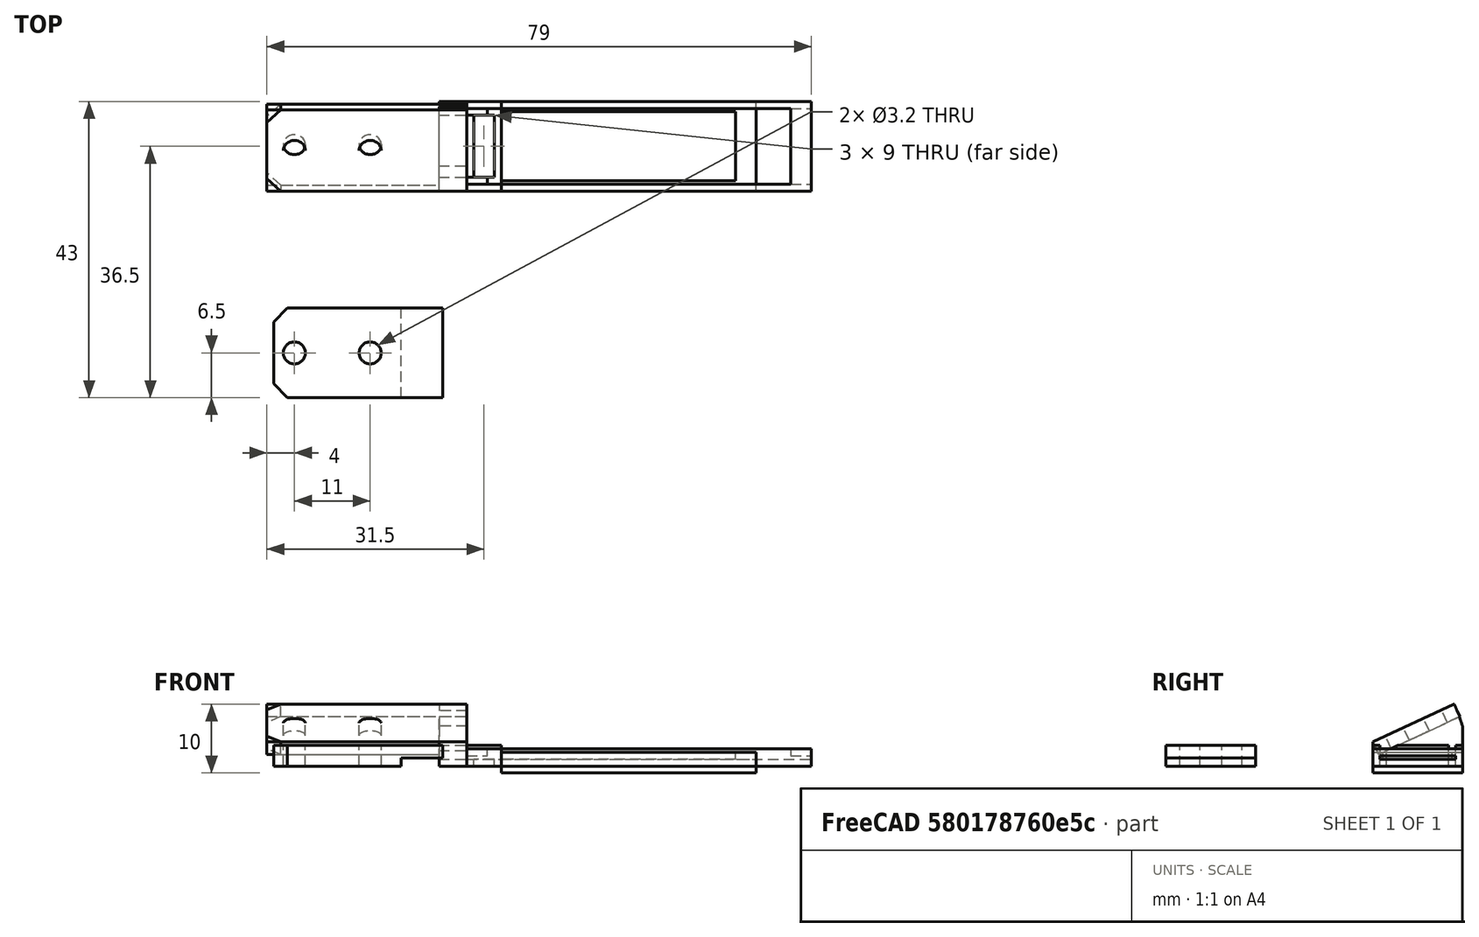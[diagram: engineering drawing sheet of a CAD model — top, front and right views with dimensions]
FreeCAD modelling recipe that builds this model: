
FCSTD DOCUMENT  (FreeCAD 0.18R14555 (Git shallow))
Label: neopixel-mount-bottom
License: All rights reserved
LicenseURL: http://en.wikipedia.org/wiki/All_rights_reserved
objects: Part::Box×18, Part::Cut×9, Part::Cylinder×5, Part::MultiFuse×3, Part::Chamfer×2, Part::Feature×1
note: 38 computed .brp shape members not serialized (recipe doc carries the construction recipe); baked Part::Feature solids carry a one-line shape summary decoded from their .brp

FEATURE [Part::Box] Box  label="Cube"
  AttacherType = Attacher::AttachEngine3D
  Height = 1
  Length = 37
  Width = 11
FEATURE [Part::Box] Box001  label="Cube001"
  AttacherType = Attacher::AttachEngine3D
  Height = 3
  Length = 37
  Placement = pos=(0,-1,-1) rot=(0,0,1;0rad)
  Width = 13
FEATURE [Part::Box] Box002  label="Cube002"
  AttacherType = Attacher::AttachEngine3D
  Height = 3
  Length = 34
  Placement = pos=(0,0.5,0) rot=(0,0,1;0rad)
  Width = 10
FEATURE [Part::Cut] Cut
  Base = -> Box001
  Tool = -> Box
FEATURE [Part::Cut] Cut001
  Base = -> Cut
  Tool = -> Box002
FEATURE [Part::Box] Box003  label="Cube003"
  AttacherType = Attacher::AttachEngine3D
  Height = 3
  Length = 5
  Placement = pos=(-5,-1,-1) rot=(0,0,1;0rad)
  Width = 13
FEATURE [Part::Box] Box004  label="Cube004"
  AttacherType = Attacher::AttachEngine3D
  Height = 2
  Length = 5
  Placement = pos=(-5,0,0) rot=(0,0,1;0rad)
  Width = 11
FEATURE [Part::Cut] Cut002
  Base = -> Box003
  Tool = -> Box004
FEATURE [Part::Box] Box005  label="Cube005"
  AttacherType = Attacher::AttachEngine3D
  Height = 10
  Length = 3
  Placement = pos=(-4,1,-1) rot=(0,0,1;0rad)
  Width = 9
FEATURE [Part::Cut] Cut003
  Base = -> Cut002
  Placement = pos=(0,0,1) rot=(0,0,1;0rad)
  Tool = -> Box005
FEATURE [Part::Cylinder] Cylinder
  Angle = 25
  AttacherType = Attacher::AttachEngine3D
  Height = 4
  Placement = pos=(-5,-8.5,-1) rot=(-0.473306,-0.742942,0.473306;1.86366rad)
  Radius = 21.3
FEATURE [Part::Box] Box006  label="Cube006"
  AttacherType = Attacher::AttachEngine3D
  Height = 2
  Length = 29
  Placement = pos=(-38,-1,0) rot=(0,0,1;0rad)
  Width = 13
FEATURE [Part::Cylinder] Cylinder001
  Angle = 360
  AttacherType = Attacher::AttachEngine3D
  Height = 10
  Placement = pos=(-23,5.5,0) rot=(0,0,1;0rad)
  Radius = 1.6
FEATURE [Part::Cylinder] Cylinder002
  Angle = 360
  AttacherType = Attacher::AttachEngine3D
  Height = 10
  Placement = pos=(-34,5.5,0) rot=(0,0,1;0rad)
  Radius = 1.6
FEATURE [Part::MultiFuse] Fusion
  Shapes = -> [Cylinder002,Cylinder001]
FEATURE [Part::Cut] Cut004
  Base = -> Box006
  Placement = pos=(4,0.75,2.11) rot=(1,0,0;0.436332rad)
  Tool = -> Fusion
FEATURE [Part::Box] Box007  label="Cube007"
  AttacherType = Attacher::AttachEngine3D
  Height = 10
  Length = 10
  Placement = pos=(-10.5,-11,-2) rot=(0,0,1;0rad)
  Width = 10
FEATURE [Part::Cut] Cut005
  Base = -> Cylinder
  Tool = -> Box007
FEATURE [Part::Box] Box008  label="Cube008"
  AttacherType = Attacher::AttachEngine3D
  Height = 10
  Length = 10
  Placement = pos=(-10.5,12,-5) rot=(0,0,1;0rad)
  Width = 10
FEATURE [Part::Cut] Cut006
  Base = -> Cut005
  Placement = pos=(0,0,1) rot=(0,0,1;0rad)
  Tool = -> Box008
FEATURE [Part::Box] Box009  label="Cube009"
  AttacherType = Attacher::AttachEngine3D
  Height = 2
  Length = 4
  Placement = pos=(-9,1,1) rot=(0,0,1;0rad)
  Width = 9
FEATURE [Part::Box] Box010  label="Cube010"
  AttacherType = Attacher::AttachEngine3D
  Height = 1
  Length = 50
  Placement = pos=(-5,-1,0) rot=(0,0,1;0rad)
  Width = 13
FEATURE [Part::Cut] Cut007
  Base = -> Cut006
  Tool = -> Box009
FEATURE [Part::Box] Box011  label="Cube011"
  AttacherType = Attacher::AttachEngine3D
  Height = 1
  Length = 3
  Placement = pos=(42,-1,1.5) rot=(0,0,1;0rad)
  Width = 13
FEATURE [Part::Box] Box012  label="Cube012"
  AttacherType = Attacher::AttachEngine3D
  Height = 2.5
  Length = 50
  Placement = pos=(-5,-1,0) rot=(0,0,1;0rad)
  Width = 1
FEATURE [Part::Box] Box013  label="Cube013"
  AttacherType = Attacher::AttachEngine3D
  Height = 2.5
  Length = 50
  Placement = pos=(-5,11,0) rot=(0,0,1;0rad)
  Width = 1
FEATURE [Part::Box] Box014  label="Cube014"
  AttacherType = Attacher::AttachEngine3D
  Height = 1
  Length = 3
  Placement = pos=(-5,-1,1.5) rot=(0,0,1;0rad)
  Width = 2
FEATURE [Part::Box] Box015  label="Cube015"
  AttacherType = Attacher::AttachEngine3D
  Height = 1
  Length = 3
  Placement = pos=(-5,10,1.5) rot=(0,0,1;0rad)
  Width = 2
FEATURE [Part::MultiFuse] Fusion001
  Shapes = -> [Box015,Box014,Box013,Box012,Box011,Cut007,Box010,Cut004]
FEATURE [Part::Feature] Fusion001001  label="Fusion002"
  shape: bbox 79 x 13 x 9.002 mm, 32 faces (baked)
FEATURE [Part::Box] Box016  label="Cube016"
  AttacherType = Attacher::AttachEngine3D
  Height = 3
  Length = 24.5
  Placement = pos=(-33,-31,0) rot=(0,0,1;0rad)
  Width = 13
FEATURE [Part::Box] Box017  label="Cube017"
  AttacherType = Attacher::AttachEngine3D
  Height = 1.2
  Length = 6
  Placement = pos=(-14.5,-31,0) rot=(0,0,1;0rad)
  Width = 13
FEATURE [Part::Cylinder] Cylinder003
  Angle = 360
  AttacherType = Attacher::AttachEngine3D
  Height = 10
  Placement = pos=(-30,-24.5,0) rot=(0,0,1;0rad)
  Radius = 1.6
FEATURE [Part::Cylinder] Cylinder004
  Angle = 360
  AttacherType = Attacher::AttachEngine3D
  Height = 10
  Placement = pos=(-19,-24.5,0) rot=(0,0,1;0rad)
  Radius = 1.6
FEATURE [Part::MultiFuse] Fusion001002
  Shapes = -> [Cylinder003,Cylinder004,Box017]
FEATURE [Part::Cut] Cut008
  Base = -> Box016
  Tool = -> Fusion001002
FEATURE [Part::Chamfer] Chamfer
  Base = -> Fusion001001
  Edges = 2 edges r=2: [Edge29,Edge40]
FEATURE [Part::Chamfer] Chamfer001
  Base = -> Cut008
  Edges = 2 edges r=2: [Edge1,Edge3]
